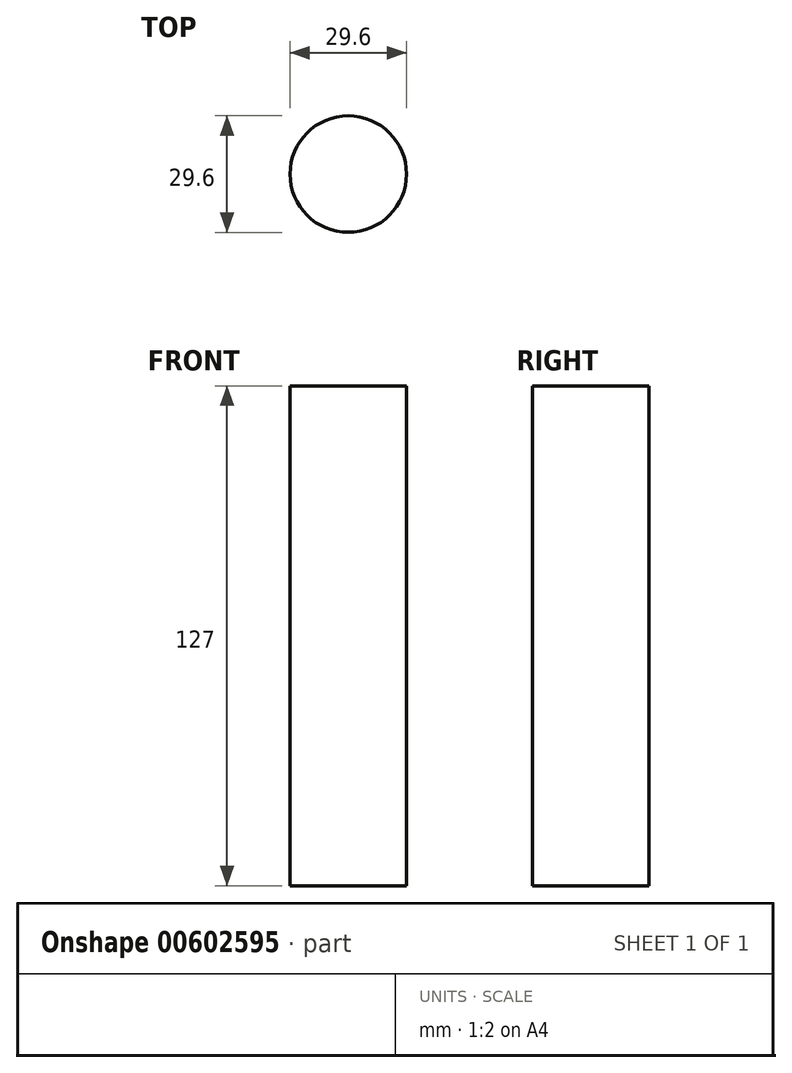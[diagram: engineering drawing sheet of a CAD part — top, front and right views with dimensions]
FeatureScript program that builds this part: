
annotation { "Feature Type Name" : "Feature", "Feature Type Description" : "" }
export const myFeature = defineFeature(function(context is Context, id is Id, definition is map)
    precondition{}
    {
        {
            var Q0;
            Q0=qCreatedBy(makeId("Top.planeOp"), FACE);
            var sketch = newSketch(context, id + "F0", { "sketchPlane" : qUnion([Q0])});
            skCircle(sketch, "E0", {"center": v(0, 0) * mm, "radius": 14.8 * mm});
            skSolve(sketch);
        }
        {
            var Q0;
            Q0 = qSketchRegion(id + "F0", true);
            extrude(context, id + "F1", {"entities" : qUnion([Q0]), "domain" : OperationDomain.MODEL, "flatOperationType" : FlatOperationType.REMOVE, "depth" : 127 * mm, "offsetDistance" : 25.4 * mm});
        }
    });
